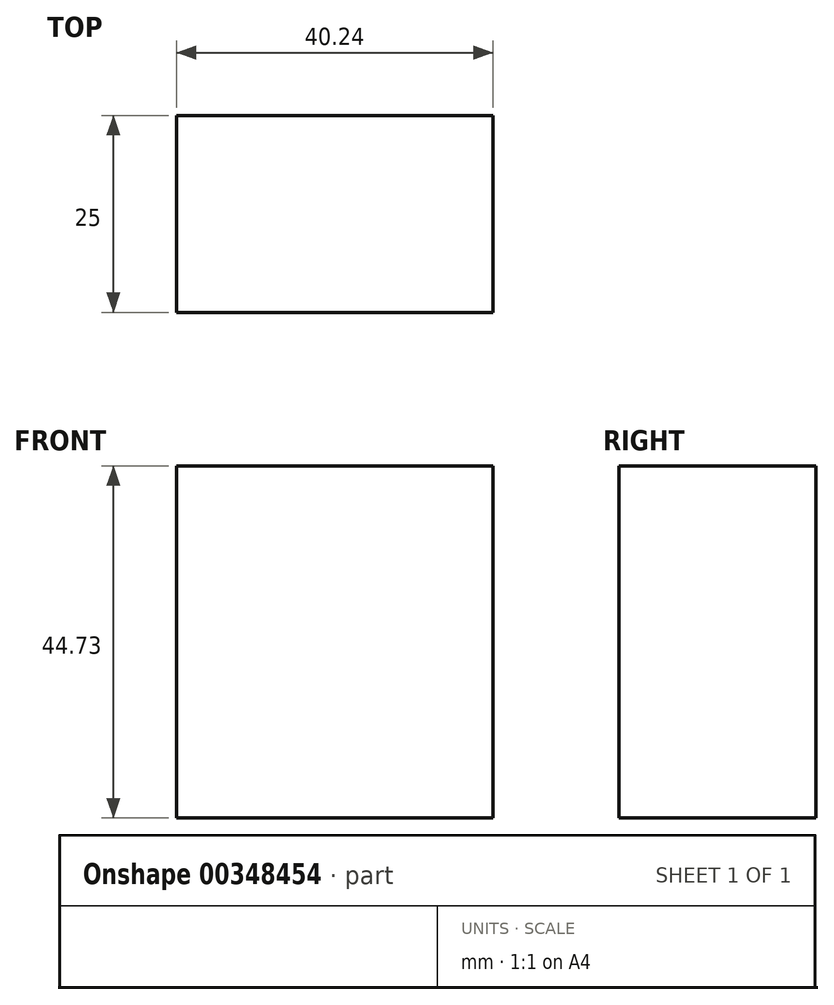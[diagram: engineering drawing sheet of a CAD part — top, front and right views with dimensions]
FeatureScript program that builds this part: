
annotation { "Feature Type Name" : "Feature", "Feature Type Description" : "" }
export const myFeature = defineFeature(function(context is Context, id is Id, definition is map)
    precondition{}
    {
        {
            var Q0;
            Q0=qCreatedBy(makeId("Front.planeOp"),FACE);
            var sketch = newSketch(context, id + "F0", { "sketchPlane" : qUnion([Q0])});
            skLineSegment(sketch, "E0.bottom", {"start": v(-73.51, 15.45) * mm, "end": v(-33.27, 15.45) * mm});
            skLineSegment(sketch, "E0.top", {"start": v(-73.51, 60.18) * mm, "end": v(-33.27, 60.18) * mm});
            skLineSegment(sketch, "E0.left", {"start": v(-73.51, 15.45) * mm, "end": v(-73.51, 60.18) * mm});
            skLineSegment(sketch, "E0.right", {"start": v(-33.27, 15.45) * mm, "end": v(-33.27, 60.18) * mm});
            skPoint(sketch, "E0.middle", {"position": v(-53.39, 37.82) * mm});
            skSolve(sketch);
        }
        {
            var Q0;
            Q0=makeQuery(id+"F0.imprint","IMPRINT",FACE,{"disambiguationData":[TD([[makeQuery(id+"F0.imprint","IMPRINT",EDGE,{"derivedFrom":sQuery(id+"F0.wireOp",EDGE,"E0.bottom")}),1.0]])]});
            extrude(context, id + "F1", {"entities" : qUnion([Q0]), "depth" : 25 * mm});
        }
    });
